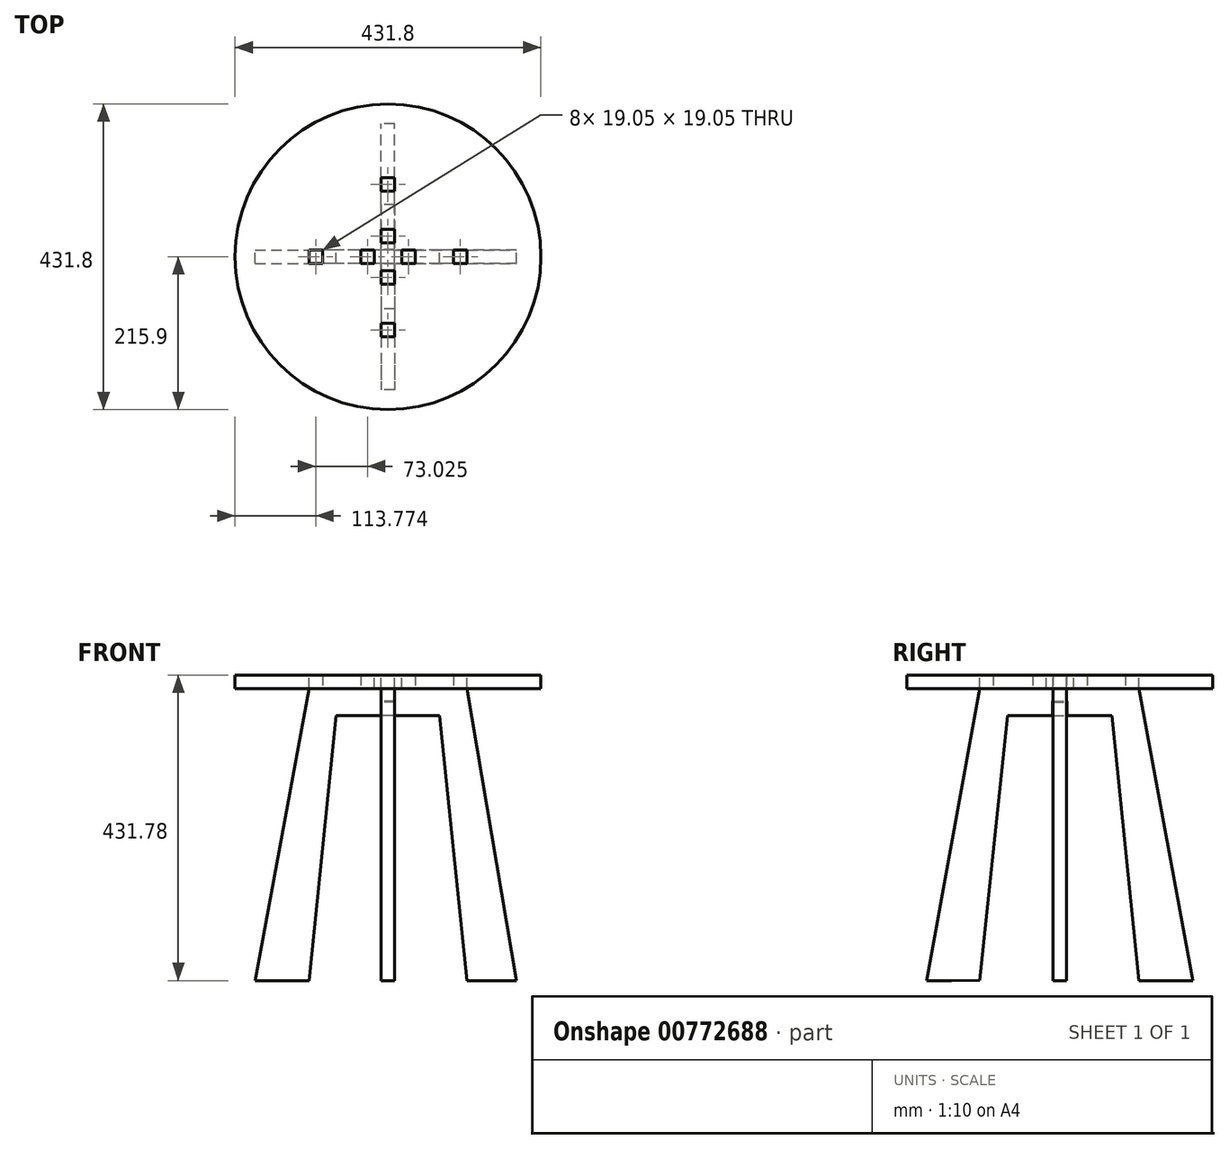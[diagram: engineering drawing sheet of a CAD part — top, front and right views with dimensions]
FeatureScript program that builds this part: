
annotation { "Feature Type Name" : "Feature", "Feature Type Description" : "" }
export const myFeature = defineFeature(function(context is Context, id is Id, definition is map)
    precondition{}
    {
        {
            var Q0;
            Q0=qCreatedBy(makeId("Top.planeOp"),FACE);
            var sketch = newSketch(context, id + "F0", { "sketchPlane" : qUnion([Q0])});
            skCircle(sketch, "E0", {"center": v(0, 0) * mm, "radius": 215.9 * mm});
            skLineSegment(sketch, "E1", {"start": v(107.95, 7.28) * mm, "end": v(107.95, 7.5) * mm});
            skPoint(sketch, "E2.orphan", {"position": v(107.95, 0) * mm});
            skPoint(sketch, "E3.start.orphan", {"position": v(115.46, 7.5) * mm});
            skPoint(sketch, "E4.end.orphan", {"position": v(115.46, 0) * mm});
            skPoint(sketch, "E5.start.orphan", {"position": v(100.44, 7.5) * mm});
            skPoint(sketch, "E6.start.orphan", {"position": v(100.44, -7.5) * mm});
            skPoint(sketch, "E7.end.orphan", {"position": v(115.46, -7.5) * mm});
            skPoint(sketch, "E7.start.orphan", {"position": v(107.95, -7.5) * mm});
            skPoint(sketch, "E8.end.orphan", {"position": v(100.44, 0) * mm});
            skSolve(sketch);
        }
        {
            var Q0;
            Q0 = qSketchRegion(id + "F0", true);
            extrude(context, id + "F1", {"entities" : qUnion([Q0]), "depth" : 19.05 * mm, "offsetDistance" : 25.4 * mm});
        }
        {
            var Q0;
            Q0=qCreatedBy(makeId("Right.planeOp"),FACE);
            var sketch = newSketch(context, id + "F2", { "sketchPlane" : qUnion([Q0])});
            skLineSegment(sketch, "E9", {"start": v(0, 0) * mm, "end": v(19.56, 0) * mm});
            skLineSegment(sketch, "E10", {"start": v(19.56, 0) * mm, "end": v(19.56, 19.05) * mm});
            skLineSegment(sketch, "E11", {"start": v(19.56, 19.05) * mm, "end": v(38.6, 19.05) * mm});
            skLineSegment(sketch, "E12", {"start": v(38.6, 19.05) * mm, "end": v(38.6, 0) * mm});
            skLineSegment(sketch, "E13", {"start": v(38.6, 0) * mm, "end": v(76.7, 0) * mm});
            skLineSegment(sketch, "E14", {"start": v(111.72, -412.73) * mm, "end": v(153, -412.73) * mm});
            skPoint(sketch, "E15.endSnap0", {"position": v(-63.86, -225.29) * mm});
            skPoint(sketch, "E16.end.orphan", {"position": v(-19.05, -38.1) * mm});
            skPoint(sketch, "E17.orphan", {"position": v(-49.58, -38.1) * mm});
            skPoint(sketch, "E18.orphan", {"position": v(-63.86, -38.1) * mm});
            skPoint(sketch, "E19.start.orphan", {"position": v(28.58, -38.08) * mm});
            skLineSegment(sketch, "E20", {"start": v(38.7, -38.08) * mm, "end": v(10.12, -38.08) * mm});
            skLineSegment(sketch, "E21", {"start": v(10.12, -38.08) * mm, "end": v(38.7, -38.08) * mm});
            skLineSegment(sketch, "E22", {"start": v(10.12, -38.08) * mm, "end": v(10.12, -19.03) * mm});
            skLineSegment(sketch, "E23", {"start": v(10.12, -19.03) * mm, "end": v(10.12, -17.76) * mm});
            skLineSegment(sketch, "E24", {"start": v(10.12, -17.76) * mm, "end": v(-0.04, -17.76) * mm});
            skPoint(sketch, "E25.orphan", {"position": v(0, -38.08) * mm});
            skPoint(sketch, "E26.orphan", {"position": v(-9.5, -38.08) * mm});
            skLineSegment(sketch, "E27.MirrorCS", {"start": v(-19.05, 0) * mm, "end": v(-19.56, 0) * mm});
            skLineSegment(sketch, "E28.MirrorCS", {"start": v(-19.56, 19.05) * mm, "end": v(-38.6, 19.05) * mm});
            skPoint(sketch, "E29.startSnap0", {"position": v(-0.04, -17.76) * mm});
            skPoint(sketch, "E30.orphan", {"position": v(0, 0) * mm});
            skPoint(sketch, "E31.start.orphan", {"position": v(-10.2, -17.76) * mm});
            skPoint(sketch, "E32.end.orphan", {"position": v(-10.2, -38.08) * mm});
            skPoint(sketch, "E33.end.orphan", {"position": v(-78.13, -412.48) * mm});
            skPoint(sketch, "E34.end.orphan", {"position": v(-78.13, 0) * mm});
            skPoint(sketch, "E35.MirrorCS.end.orphan", {"position": v(-19.56, 19.05) * mm});
            skPoint(sketch, "E35.MirrorCS.start.orphan", {"position": v(-19.56, 0) * mm});
            skPoint(sketch, "E29.start.orphan", {"position": v(0, -17.76) * mm});
            skLineSegment(sketch, "E36.MirrorCS", {"start": v(-10.12, -38.08) * mm, "end": v(-38.7, -38.08) * mm});
            skLineSegment(sketch, "E37.MirrorCS", {"start": v(-38.7, -38.08) * mm, "end": v(-10.12, -38.08) * mm});
            skLineSegment(sketch, "E38.MirrorCS", {"start": v(-10.12, -19.03) * mm, "end": v(-10.12, -17.76) * mm});
            skLineSegment(sketch, "E39.MirrorCS", {"start": v(-10.12, -38.08) * mm, "end": v(-10.12, -19.03) * mm});
            skLineSegment(sketch, "E40.MirrorCS", {"start": v(-19.56, 0) * mm, "end": v(-19.56, 19.05) * mm});
            skLineSegment(sketch, "E41.MirrorCS", {"start": v(-38.6, 19.05) * mm, "end": v(-38.6, 0) * mm});
            skPoint(sketch, "E42.MirrorP", {"position": v(10.2, -38.08) * mm});
            skLineSegment(sketch, "E43.MirrorCS", {"start": v(-38.6, 0) * mm, "end": v(-76.7, 0) * mm});
            skPoint(sketch, "E44.MirrorP", {"position": v(-28.58, -38.08) * mm});
            skPoint(sketch, "E45.MirrorP", {"position": v(9.5, -38.08) * mm});
            skPoint(sketch, "E46.MirrorP", {"position": v(10.2, -17.76) * mm});
            skLineSegment(sketch, "E47", {"start": v(-10.12, -17.76) * mm, "end": v(0, -17.76) * mm});
            skLineSegment(sketch, "E48", {"start": v(0, 0) * mm, "end": v(-19.56, 0) * mm});
            skPoint(sketch, "E49.end.orphan", {"position": v(111.72, 0) * mm});
            skLineSegment(sketch, "E50", {"start": v(-78.13, 0) * mm, "end": v(-94, 0) * mm});
            skLineSegment(sketch, "E51", {"start": v(76.7, 0) * mm, "end": v(92.67, 0) * mm});
            skPoint(sketch, "E52.end.orphan", {"position": v(-73.53, 0) * mm});
            skLineSegment(sketch, "E53", {"start": v(-153, -412.73) * mm, "end": v(-187.92, -412.73) * mm});
            skLineSegment(sketch, "E54", {"start": v(-113.06, 0) * mm, "end": v(-187.92, -412.73) * mm});
            skLineSegment(sketch, "E55", {"start": v(-38.7, -38.08) * mm, "end": v(-73.62, -38.08) * mm});
            skLineSegment(sketch, "E56", {"start": v(-73.62, -38.08) * mm, "end": v(-113.06, -412.48) * mm});
            skPoint(sketch, "E57.MirrorCS.start.orphan", {"position": v(-76.8, -412.73) * mm});
            skLineSegment(sketch, "E58", {"start": v(-113.06, -412.48) * mm, "end": v(-153, -412.73) * mm});
            skLineSegment(sketch, "E59", {"start": v(153, -412.73) * mm, "end": v(187.92, -412.73) * mm});
            skLineSegment(sketch, "E60", {"start": v(111.72, 0) * mm, "end": v(187.92, -412.73) * mm});
            skLineSegment(sketch, "E61", {"start": v(38.7, -38.08) * mm, "end": v(73.62, -38.08) * mm});
            skLineSegment(sketch, "E62", {"start": v(73.62, -38.08) * mm, "end": v(111.72, -412.73) * mm});
            skPoint(sketch, "E63.start.orphan", {"position": v(76.8, -412.73) * mm});
            skLineSegment(sketch, "E64", {"start": v(111.72, 0) * mm, "end": v(111.72, 19.05) * mm});
            skLineSegment(sketch, "E65", {"start": v(111.72, 19.05) * mm, "end": v(92.67, 19.05) * mm});
            skLineSegment(sketch, "E66", {"start": v(92.67, 19.05) * mm, "end": v(92.67, 0) * mm});
            skLineSegment(sketch, "E67", {"start": v(-113.06, 0) * mm, "end": v(-113.06, 19.05) * mm});
            skLineSegment(sketch, "E68", {"start": v(-113.06, 19.05) * mm, "end": v(-94, 19.05) * mm});
            skLineSegment(sketch, "E69", {"start": v(-94, 19.05) * mm, "end": v(-94, 0) * mm});
            skLineSegment(sketch, "E70", {"start": v(92.67, 0) * mm, "end": v(38.6, 0) * mm});
            skLineSegment(sketch, "E71", {"start": v(-38.6, 0) * mm, "end": v(-94, 0) * mm});
            skSolve(sketch);
        }
        {
            var Q0;
            Q0=qCreatedBy(makeId("Front.planeOp"),FACE);
            var sketch = newSketch(context, id + "F3", { "sketchPlane" : qUnion([Q0])});
            skLineSegment(sketch, "E72", {"start": v(9.51, 0) * mm, "end": v(9.51, -19.05) * mm});
            skLineSegment(sketch, "E73", {"start": v(9.51, -19.05) * mm, "end": v(-9.55, -19.05) * mm});
            skLineSegment(sketch, "E74", {"start": v(-9.55, -19.05) * mm, "end": v(-9.54, 0) * mm});
            skLineSegment(sketch, "E75", {"start": v(-9.54, 0) * mm, "end": v(-19.58, 0) * mm});
            skLineSegment(sketch, "E76", {"start": v(9.51, 0) * mm, "end": v(19.55, 0) * mm});
            skLineSegment(sketch, "E77", {"start": v(19.55, 0) * mm, "end": v(19.55, 19.05) * mm});
            skLineSegment(sketch, "E78", {"start": v(19.55, 19.05) * mm, "end": v(38.6, 19.05) * mm});
            skLineSegment(sketch, "E79", {"start": v(38.6, 19.05) * mm, "end": v(38.6, 0) * mm});
            skLineSegment(sketch, "E80", {"start": v(38.6, 0) * mm, "end": v(76.7, 0) * mm});
            skLineSegment(sketch, "E81", {"start": v(-19.58, 0) * mm, "end": v(-19.58, 19.05) * mm});
            skLineSegment(sketch, "E82", {"start": v(-19.58, 19.05) * mm, "end": v(-38.63, 19.05) * mm});
            skLineSegment(sketch, "E83", {"start": v(-38.63, 19.05) * mm, "end": v(-38.63, 0) * mm});
            skLineSegment(sketch, "E84", {"start": v(-38.63, 0) * mm, "end": v(-76.73, 0) * mm});
            skLineSegment(sketch, "E85", {"start": v(111.62, -412.73) * mm, "end": v(146.55, -412.73) * mm});
            skLineSegment(sketch, "E86", {"start": v(9.51, -38.1) * mm, "end": v(38.09, -38.1) * mm});
            skLineSegment(sketch, "E87", {"start": v(9.51, -38.1) * mm, "end": v(-9.54, -38.1) * mm});
            skLineSegment(sketch, "E88", {"start": v(-9.54, -38.1) * mm, "end": v(-38.11, -38.1) * mm});
            skLineSegment(sketch, "E89", {"start": v(-111.65, -412.72) * mm, "end": v(-152.93, -412.72) * mm});
            skLineSegment(sketch, "E90", {"start": v(-76.73, 0) * mm, "end": v(-92.6, 0) * mm});
            skLineSegment(sketch, "E91", {"start": v(-152.93, -412.72) * mm, "end": v(-187.85, -412.72) * mm});
            skLineSegment(sketch, "E92", {"start": v(-187.85, -412.72) * mm, "end": v(-111.65, 0) * mm});
            skLineSegment(sketch, "E93", {"start": v(-38.11, -38.1) * mm, "end": v(-73.04, -38.1) * mm});
            skLineSegment(sketch, "E94", {"start": v(-73.04, -38.1) * mm, "end": v(-111.65, -412.72) * mm});
            skLineSegment(sketch, "E95", {"start": v(-111.65, 0) * mm, "end": v(-111.65, 19.05) * mm});
            skLineSegment(sketch, "E96", {"start": v(-111.65, 19.05) * mm, "end": v(-92.6, 19.05) * mm});
            skLineSegment(sketch, "E97", {"start": v(-92.6, 19.05) * mm, "end": v(-92.6, 0) * mm});
            skLineSegment(sketch, "E98", {"start": v(-92.6, 0) * mm, "end": v(-76.73, 0) * mm});
            skLineSegment(sketch, "E99", {"start": v(146.55, -412.73) * mm, "end": v(181.47, -412.73) * mm});
            skLineSegment(sketch, "E100", {"start": v(181.47, -412.73) * mm, "end": v(111.62, 0) * mm});
            skLineSegment(sketch, "E101", {"start": v(38.09, -38.1) * mm, "end": v(73.01, -38.1) * mm});
            skLineSegment(sketch, "E102", {"start": v(111.62, -412.73) * mm, "end": v(181.47, -412.73) * mm});
            skLineSegment(sketch, "E103", {"start": v(111.62, -412.73) * mm, "end": v(73.01, -38.1) * mm});
            skPoint(sketch, "E104.start.orphan", {"position": v(76.7, -412.73) * mm});
            skLineSegment(sketch, "E105", {"start": v(111.62, 0) * mm, "end": v(111.62, 19.05) * mm});
            skLineSegment(sketch, "E106", {"start": v(111.62, 19.05) * mm, "end": v(92.57, 19.05) * mm});
            skLineSegment(sketch, "E107", {"start": v(92.57, 19.05) * mm, "end": v(92.57, 0) * mm});
            skLineSegment(sketch, "E108", {"start": v(92.57, 0) * mm, "end": v(76.7, 0) * mm});
            skSolve(sketch);
        }
        {
            var Q0;
            Q0 = qSketchRegion(id + "F3", true);
            extrude(context, id + "F4", {"entities" : qUnion([Q0]), "endBound" : BoundingType.SYMMETRIC, "depth" : 19.05 * mm, "offsetDistance" : 25.4 * mm});
        }
        {
            var Q0;
            Q0 = qSketchRegion(id + "F2", true);
            extrude(context, id + "F5", {"entities" : qUnion([Q0]), "endBound" : BoundingType.SYMMETRIC, "depth" : 19.05 * mm, "offsetDistance" : 25.4 * mm});
        }
        {
            var Q0;
            Q0 = qSketchRegion(id + "F3", true);
            extrude(context, id + "F6", {"entities" : qUnion([Q0]), "endBound" : BoundingType.SYMMETRIC, "depth" : 19.05 * mm, "offsetDistance" : 25.4 * mm});
        }
        {
            var Q0;
            Q0=makeQuery(id+"F6.opExtrude","SWEPT_BODY",BODY,{"disambiguationData":[OSD([sQuery(id+"F3.wireOp",EDGE,"E72"),sQuery(id+"F3.wireOp",EDGE,"E73"),sQuery(id+"F3.wireOp",EDGE,"E74"),sQuery(id+"F3.wireOp",EDGE,"E75"),sQuery(id+"F3.wireOp",EDGE,"E76"),sQuery(id+"F3.wireOp",EDGE,"E77"),sQuery(id+"F3.wireOp",EDGE,"E78"),sQuery(id+"F3.wireOp",EDGE,"E79"),sQuery(id+"F3.wireOp",EDGE,"E80"),sQuery(id+"F3.wireOp",EDGE,"E81"),sQuery(id+"F3.wireOp",EDGE,"E82"),sQuery(id+"F3.wireOp",EDGE,"E83"),sQuery(id+"F3.wireOp",EDGE,"E84"),sQuery(id+"F3.wireOp",EDGE,"E85"),sQuery(id+"F3.wireOp",EDGE,"E86"),sQuery(id+"F3.wireOp",EDGE,"E87"),sQuery(id+"F3.wireOp",EDGE,"E88"),sQuery(id+"F3.wireOp",EDGE,"E89"),sQuery(id+"F3.wireOp",EDGE,"E91"),sQuery(id+"F3.wireOp",EDGE,"E92"),sQuery(id+"F3.wireOp",EDGE,"E93"),sQuery(id+"F3.wireOp",EDGE,"E94"),sQuery(id+"F3.wireOp",EDGE,"E95"),sQuery(id+"F3.wireOp",EDGE,"E96"),sQuery(id+"F3.wireOp",EDGE,"E97"),sQuery(id+"F3.wireOp",EDGE,"E98"),sQuery(id+"F3.wireOp",EDGE,"E100"),sQuery(id+"F3.wireOp",EDGE,"E101"),sQuery(id+"F3.wireOp",EDGE,"E102"),sQuery(id+"F3.wireOp",EDGE,"E103"),sQuery(id+"F3.wireOp",EDGE,"E105"),sQuery(id+"F3.wireOp",EDGE,"E106"),sQuery(id+"F3.wireOp",EDGE,"E107"),sQuery(id+"F3.wireOp",EDGE,"E108")])]});
            deleteBodies(context, id + "F7", {"entities" : qUnion([Q0])});
        }
        {
            var Q0;
            Q0=makeQuery(id+"F5.opExtrude","SWEPT_BODY",BODY,{"disambiguationData":[OSD([sQuery(id+"F2.wireOp",EDGE,"E9"),sQuery(id+"F2.wireOp",EDGE,"E10"),sQuery(id+"F2.wireOp",EDGE,"E11"),sQuery(id+"F2.wireOp",EDGE,"E12"),sQuery(id+"F2.wireOp",EDGE,"E14"),sQuery(id+"F2.wireOp",EDGE,"E22"),sQuery(id+"F2.wireOp",EDGE,"E23"),sQuery(id+"F2.wireOp",EDGE,"E24"),sQuery(id+"F2.wireOp",EDGE,"E21"),sQuery(id+"F2.wireOp",EDGE,"E38.MirrorCS"),sQuery(id+"F2.wireOp",EDGE,"E37.MirrorCS"),sQuery(id+"F2.wireOp",EDGE,"E39.MirrorCS"),sQuery(id+"F2.wireOp",EDGE,"E28.MirrorCS"),sQuery(id+"F2.wireOp",EDGE,"E40.MirrorCS"),sQuery(id+"F2.wireOp",EDGE,"E41.MirrorCS"),sQuery(id+"F2.wireOp",EDGE,"E47"),sQuery(id+"F2.wireOp",EDGE,"E48"),sQuery(id+"F2.wireOp",EDGE,"E53"),sQuery(id+"F2.wireOp",EDGE,"E54"),sQuery(id+"F2.wireOp",EDGE,"E55"),sQuery(id+"F2.wireOp",EDGE,"E56"),sQuery(id+"F2.wireOp",EDGE,"E58"),sQuery(id+"F2.wireOp",EDGE,"E59"),sQuery(id+"F2.wireOp",EDGE,"E60"),sQuery(id+"F2.wireOp",EDGE,"E61"),sQuery(id+"F2.wireOp",EDGE,"E62"),sQuery(id+"F2.wireOp",EDGE,"E64"),sQuery(id+"F2.wireOp",EDGE,"E65"),sQuery(id+"F2.wireOp",EDGE,"E66"),sQuery(id+"F2.wireOp",EDGE,"E67"),sQuery(id+"F2.wireOp",EDGE,"E68"),sQuery(id+"F2.wireOp",EDGE,"E69"),sQuery(id+"F2.wireOp",EDGE,"E70"),sQuery(id+"F2.wireOp",EDGE,"E71")])]});
            var Q1;
            Q1=makeQuery(id+"F4.opExtrude","SWEPT_BODY",BODY,{"disambiguationData":[OSD([sQuery(id+"F3.wireOp",EDGE,"E72"),sQuery(id+"F3.wireOp",EDGE,"E73"),sQuery(id+"F3.wireOp",EDGE,"E74"),sQuery(id+"F3.wireOp",EDGE,"E75"),sQuery(id+"F3.wireOp",EDGE,"E76"),sQuery(id+"F3.wireOp",EDGE,"E77"),sQuery(id+"F3.wireOp",EDGE,"E78"),sQuery(id+"F3.wireOp",EDGE,"E79"),sQuery(id+"F3.wireOp",EDGE,"E80"),sQuery(id+"F3.wireOp",EDGE,"E81"),sQuery(id+"F3.wireOp",EDGE,"E82"),sQuery(id+"F3.wireOp",EDGE,"E83"),sQuery(id+"F3.wireOp",EDGE,"E84"),sQuery(id+"F3.wireOp",EDGE,"E85"),sQuery(id+"F3.wireOp",EDGE,"E86"),sQuery(id+"F3.wireOp",EDGE,"E87"),sQuery(id+"F3.wireOp",EDGE,"E88"),sQuery(id+"F3.wireOp",EDGE,"E89"),sQuery(id+"F3.wireOp",EDGE,"E91"),sQuery(id+"F3.wireOp",EDGE,"E92"),sQuery(id+"F3.wireOp",EDGE,"E93"),sQuery(id+"F3.wireOp",EDGE,"E94"),sQuery(id+"F3.wireOp",EDGE,"E95"),sQuery(id+"F3.wireOp",EDGE,"E96"),sQuery(id+"F3.wireOp",EDGE,"E97"),sQuery(id+"F3.wireOp",EDGE,"E98"),sQuery(id+"F3.wireOp",EDGE,"E100"),sQuery(id+"F3.wireOp",EDGE,"E101"),sQuery(id+"F3.wireOp",EDGE,"E102"),sQuery(id+"F3.wireOp",EDGE,"E103"),sQuery(id+"F3.wireOp",EDGE,"E105"),sQuery(id+"F3.wireOp",EDGE,"E106"),sQuery(id+"F3.wireOp",EDGE,"E107"),sQuery(id+"F3.wireOp",EDGE,"E108")])]});
            var Q2;
            Q2=makeQuery(id+"F1.opExtrude","SWEPT_BODY",BODY,{"disambiguationData":[OSD([sQuery(id+"F0.wireOp",EDGE,"E0")])]});
            booleanBodies(context, id + "F8", {"operationType" : BooleanOperationType.SUBTRACTION, "tools" : qUnion([Q0, Q1]), "targets" : qUnion([Q2]), "keepTools" : true});
        }
    });
